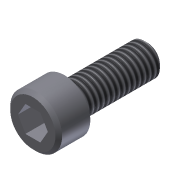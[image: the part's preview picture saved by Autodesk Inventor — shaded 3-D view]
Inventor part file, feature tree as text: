
AUTODESK INVENTOR PART (.ipt)
format: ipt  version: 2011 SP1 (Build 150282100, 282)  size: 107,520 bytes
history: native  units: in
note: dims shown in document units (in); Inventor stores cm internally (conversion verified against a paired STEP export)
features: extrude x3, sketch x3, chamfer x2, thread x1
ambient origin geometry x8: Origin, YZ Plane, XZ Plane, XY Plane, X Axis, Y Axis, Z Axis, Center Point
bodies: Solid1 (feature_tree)
feature tree (9):
  extrude  "Extrusion1"  Depth=0.19in TaperAngle=0.0deg
  extrude  "Extrusion2"  Depth=0.5in TaperAngle=0.0deg
  extrude  "Extrusion3"  Depth=0.125in TaperAngle=0.0deg
  thread  "Thread1"  [1 undecoded]
  chamfer  "Chamfer1"  Distance=0.02in Angle=45.0deg
  chamfer  "Chamfer2"  Distance=0.02in Angle=45.0deg
  sketch  "Sketch1"  dims[d0=0.312in d1=0.19in d2=0.0in]
  sketch  "Sketch2"  dims[d3=0.19in d4=0.5in d5=0.0in]
  sketch  "Sketch3"  dims[d6=0.1562in d7=0.125in d8=0.0in d9=1.0in d10=0.0in d11=0.02in d12=0.125in d13=45.0deg d14=0.02in d15=0.125in d16=45.0deg]
note: 1 required parameter value undecoded (feature->parameter linkage not recoverable at this tier; creation-order binding heuristic only, values carry confidence <= 0.55)
